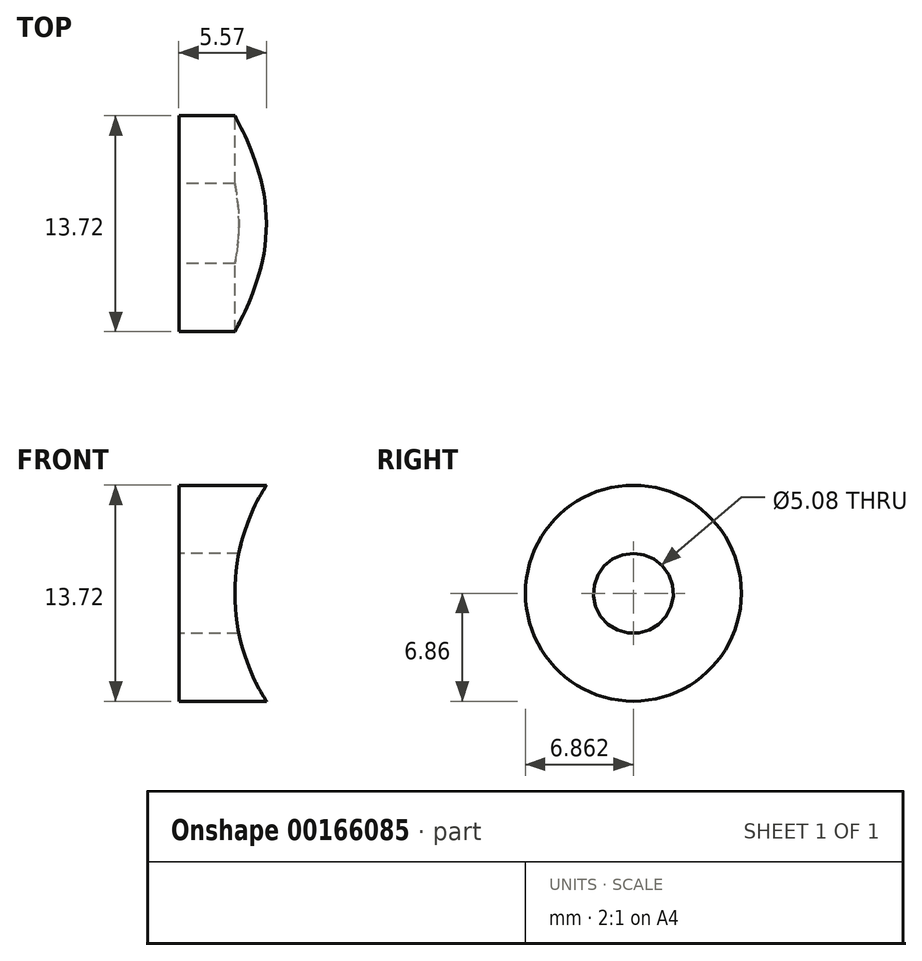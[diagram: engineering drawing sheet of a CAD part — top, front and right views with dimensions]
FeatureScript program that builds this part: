
annotation { "Feature Type Name" : "Feature", "Feature Type Description" : "" }
export const myFeature = defineFeature(function(context is Context, id is Id, definition is map)
    precondition{}
    {
        {
            var Q0;
            Q0=qCreatedBy(makeId("Front.planeOp"),FACE);
            var sketch = newSketch(context, id + "F0", { "sketchPlane" : qUnion([Q0])});
            skCircle(sketch, "E0", {"center": v(0, 0) * mm, "radius": 12.7 * mm});
            skLineSegment(sketch, "E1", {"start": v(-16.26, 0) * mm, "end": v(-16.26, 6.86) * mm});
            skLineSegment(sketch, "E2", {"start": v(-16.26, 6.86) * mm, "end": v(-10.69, 6.86) * mm});
            skLineSegment(sketch, "E3.MirrorCS", {"start": v(-16.26, 0) * mm, "end": v(-16.26, -6.86) * mm});
            skLineSegment(sketch, "E4.MirrorCS", {"start": v(-16.26, -6.86) * mm, "end": v(-10.69, -6.86) * mm});
            skSolve(sketch);
        }
        {
            var Q0;
            Q0=makeQuery(id+"F0.imprint","IMPRINT",FACE,{"disambiguationData":[TD([[makeQuery(id+"F0.imprint","IMPRINT",EDGE,{"derivedFrom":sQuery(id+"F0.wireOp",EDGE,"E1")}),-1.0]])]});
            extrude(context, id + "F1", {"entities" : qUnion([Q0]), "depth" : 13.72 * mm});
        }
        {
            var Q0;
            Q0=makeQuery(id+"F1.opExtrude","CAP_EDGE",EDGE,{"disambiguationData":[OSD([sQuery(id+"F0.wireOp",EDGE,"E2")])],"isStart":true});
            var Q1;
            Q1=makeQuery(id+"F1.opExtrude","CAP_EDGE",EDGE,{"disambiguationData":[OSD([sQuery(id+"F0.wireOp",EDGE,"E2")])],"isStart":false});
            var Q2;
            Q2=makeQuery(id+"F1.opExtrude","CAP_EDGE",EDGE,{"disambiguationData":[OSD([sQuery(id+"F0.wireOp",EDGE,"E4.MirrorCS")])],"isStart":false});
            var Q3;
            Q3=makeQuery(id+"F1.opExtrude","CAP_EDGE",EDGE,{"disambiguationData":[OSD([sQuery(id+"F0.wireOp",EDGE,"E4.MirrorCS")])],"isStart":true});
            fillet(context, id + "F2", {"entities" : qUnion([Q0, Q1, Q2, Q3]), "radius" : 6.86 * mm, "tangentPropagation" : true, "allowEdgeOverflow" : false});
        }
        {
            var Q0;
            Q0=makeQuery(id+"F1.opExtrude","SWEPT_FACE",FACE,{"disambiguationData":[OSD([sQuery(id+"F0.wireOp",EDGE,"E1"),sQuery(id+"F0.wireOp",EDGE,"E3.MirrorCS")])]});
            var sketch = newSketch(context, id + "F3", { "sketchPlane" : qUnion([Q0])});
            skPoint(sketch, "E5", {"position": v(6.86, 0) * mm});
            skCircle(sketch, "E6", {"center": v(6.86, 0) * mm, "radius": 2.54 * mm});
            skSolve(sketch);
        }
        {
            var Q0;
            Q0=makeQuery(id+"F3.imprint","IMPRINT",FACE,{"disambiguationData":[TD([[makeQuery(id+"F3.imprint","IMPRINT",EDGE,{"derivedFrom":sQuery(id+"F3.wireOp",EDGE,"E6")}),1.0]])]});
            extrude(context, id + "F4", {"entities" : qUnion([Q0]), "operationType" : NewBodyOperationType.REMOVE, "endBound" : BoundingType.THROUGH_ALL, "oppositeDirection" : true, "depth" : 25.4 * mm});
        }
    });
